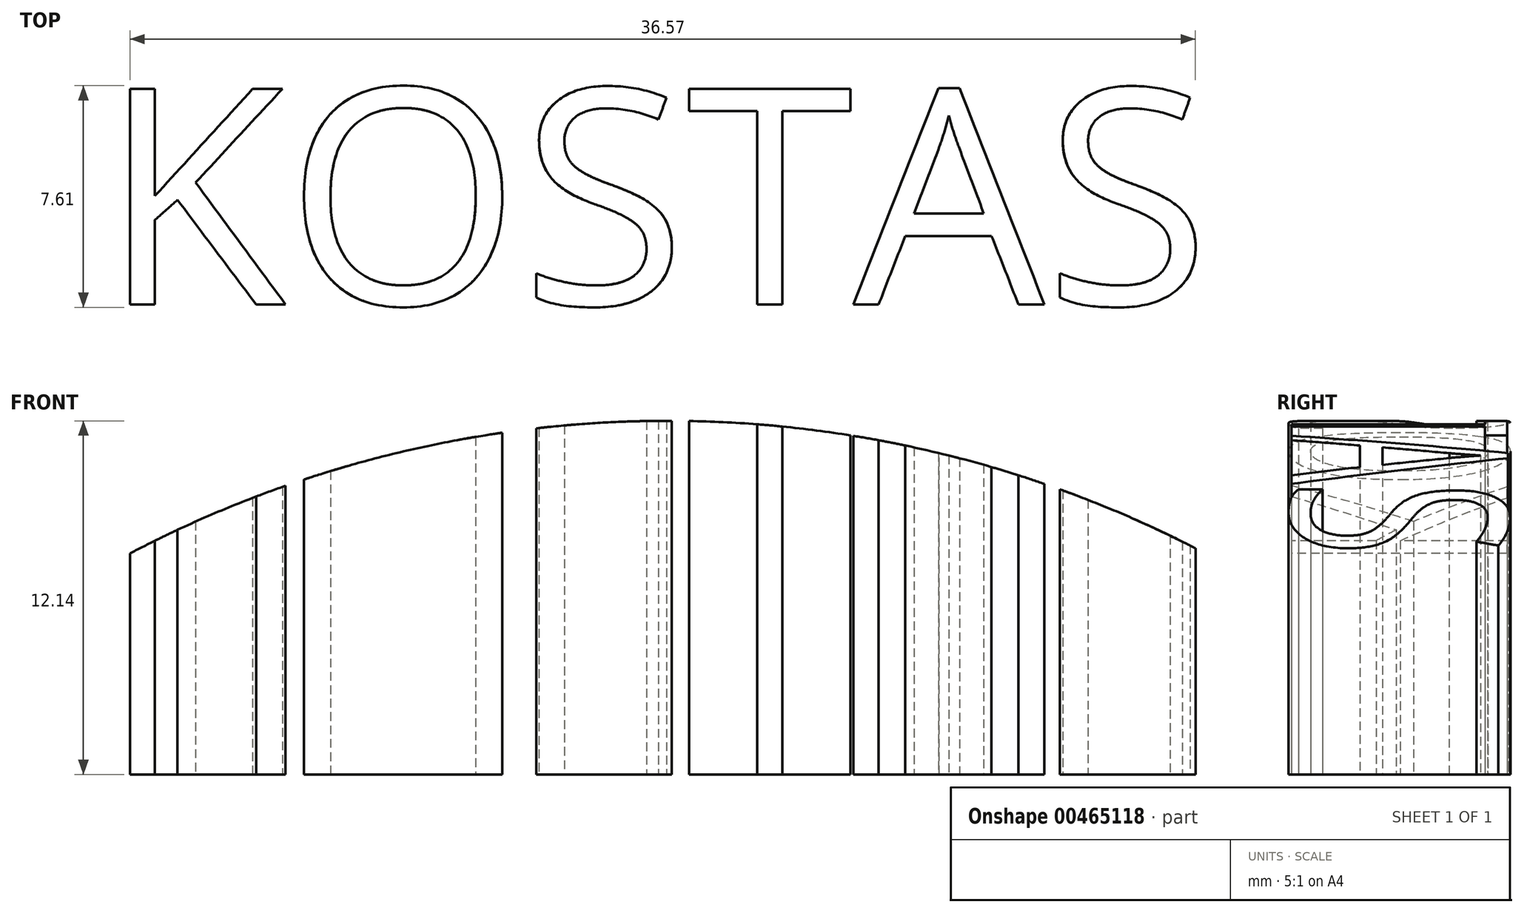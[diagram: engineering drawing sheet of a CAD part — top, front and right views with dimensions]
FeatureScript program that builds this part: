
annotation { "Feature Type Name" : "Feature", "Feature Type Description" : "" }
export const myFeature = defineFeature(function(context is Context, id is Id, definition is map)
    precondition{}
    {
        {
            var Q0;
            Q0=qCreatedBy(makeId("Top.planeOp"),FACE);
            var sketch = newSketch(context, id + "F0", { "sketchPlane" : qUnion([Q0])});
            skLineSegment(sketch, "E0", {"start": v(0, 0) * mm, "end": v(42.2, 0) * mm, "construction": true});
            skText(sketch, "E1", { "text": "KOSTAS", "fontName": "OpenSans-Regular.ttf"});
            const initialGuessF0  = {"E1": [0.00249, 0, 1, 0, 0.00746]};
            skSetInitialGuess(sketch, initialGuessF0);
            skSolve(sketch);
        }
        {
            var Q0;
            Q0 = qSketchRegion(id + "F0", true);
            var Q1;
            Q1=sQuery(id+"F0.wireOp",EDGE,"E0");
            extrude(context, id + "F1", {"entities" : qUnion([Q0]), "surfaceEntities" : qUnion([Q1]), "depth" : 12.7 * mm});
        }
        {
            var Q0;
            Q0=qCreatedBy(makeId("Front.planeOp"),FACE);
            var sketch = newSketch(context, id + "F2", { "sketchPlane" : qUnion([Q0])});
            skCircle(sketch, "E2", {"center": v(21.97, -27.54) * mm, "radius": 39.68 * mm});
            skLineSegment(sketch, "E3", {"start": v(-8.83, -2.52) * mm, "end": v(-8.83, 32.54) * mm});
            skLineSegment(sketch, "E4", {"start": v(-8.83, 32.54) * mm, "end": v(51.57, 18.96) * mm});
            skLineSegment(sketch, "E5", {"start": v(51.57, 18.96) * mm, "end": v(45.6, 4.33) * mm});
            skSolve(sketch);
        }
        {
            var Q0;
            {var subQ0=sQuery(id+"F2.wireOp",EDGE,"E3");Q0=makeQuery(id+"F2.imprint","IMPRINT",FACE,{"disambiguationData":[TD([[makeQuery(id+"F2.imprint","IMPRINT",EDGE,{"derivedFrom":subQ0}),-1.0]])]});}
            extrude(context, id + "F3", {"entities" : qUnion([Q0]), "operationType" : NewBodyOperationType.REMOVE, "endBound" : BoundingType.SYMMETRIC, "oppositeDirection" : true, "depth" : 25.4 * mm});
        }
    });
